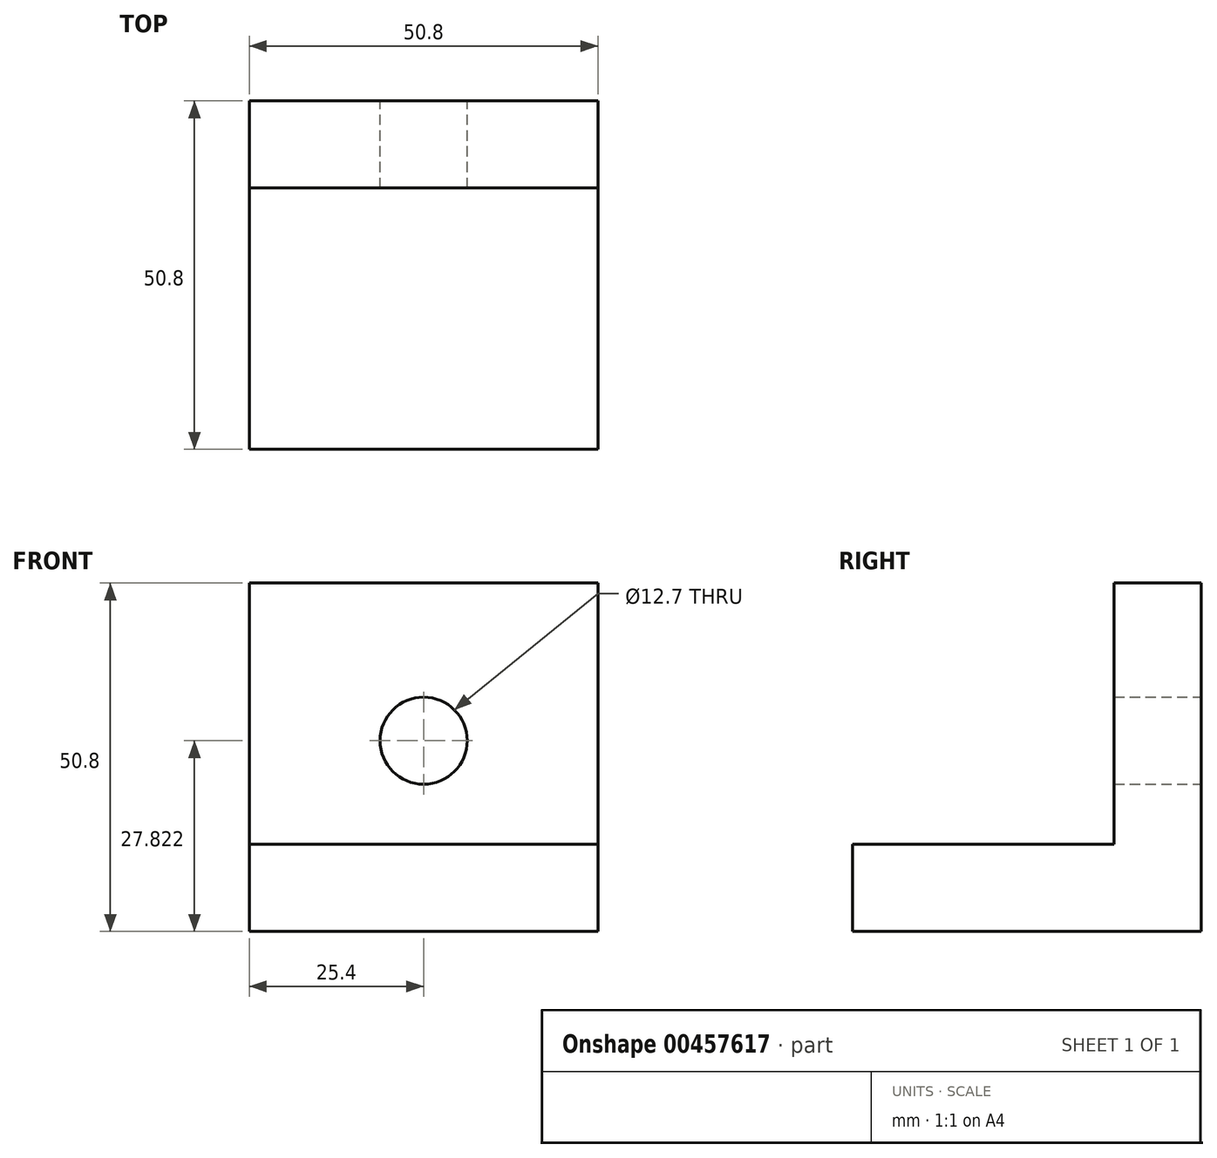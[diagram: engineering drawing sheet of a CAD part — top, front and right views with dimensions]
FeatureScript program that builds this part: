
annotation { "Feature Type Name" : "Feature", "Feature Type Description" : "" }
export const myFeature = defineFeature(function(context is Context, id is Id, definition is map)
    precondition{}
    {
        {
            var Q0;
            Q0=qCreatedBy(makeId("Right.planeOp"),FACE);
            var sketch = newSketch(context, id + "F0", { "sketchPlane" : qUnion([Q0])});
            skLineSegment(sketch, "E0", {"start": v(0, 33.78) * mm, "end": v(0, -17.02) * mm});
            skLineSegment(sketch, "E1", {"start": v(0, -17.02) * mm, "end": v(-50.8, -17.02) * mm});
            skLineSegment(sketch, "E2", {"start": v(-50.8, -17.02) * mm, "end": v(-50.8, -4.32) * mm});
            skLineSegment(sketch, "E3", {"start": v(-50.8, -4.32) * mm, "end": v(-12.7, -4.32) * mm});
            skLineSegment(sketch, "E4", {"start": v(-12.7, -4.32) * mm, "end": v(-12.7, 33.78) * mm});
            skLineSegment(sketch, "E5", {"start": v(-12.7, 33.78) * mm, "end": v(0, 33.78) * mm});
            skSolve(sketch);
        }
        {
            var Q0;
            Q0=qCreatedBy(makeId("Front.planeOp"),FACE);
            var sketch = newSketch(context, id + "F1", { "sketchPlane" : qUnion([Q0])});
            skCircle(sketch, "E6", {"center": v(0, 10.8) * mm, "radius": 6.35 * mm});
            skSolve(sketch);
        }
        {
            var Q0;
            Q0=makeQuery(id+"F0.imprint","IMPRINT",FACE,{"disambiguationData":[TD([[makeQuery(id+"F0.imprint","IMPRINT",EDGE,{"derivedFrom":sQuery(id+"F0.wireOp",EDGE,"E0")}),-1.0]])]});
            extrude(context, id + "F2", {"entities" : qUnion([Q0]), "endBound" : BoundingType.SYMMETRIC, "depth" : 50.8 * mm});
        }
        {
            var Q0;
            Q0=sQuery(id+"F1.wireOp",VERTEX,"E6.center");
            var Q1;
            Q1=makeQuery(id+"F2.opExtrude","SWEPT_BODY",BODY,{"disambiguationData":[OSD([sQuery(id+"F0.wireOp",EDGE,"E0"),sQuery(id+"F0.wireOp",EDGE,"E1"),sQuery(id+"F0.wireOp",EDGE,"E2"),sQuery(id+"F0.wireOp",EDGE,"E3"),sQuery(id+"F0.wireOp",EDGE,"E4"),sQuery(id+"F0.wireOp",EDGE,"E5")])]});
            hole(context, id + "F3", {"style" : HoleStyle.SIMPLE, "endStyle" : HoleEndStyle.THROUGH, "oppositeDirection" : true, "holeDiameter" : 12.7 * mm, "isTappedThrough" : true, "tappedDepth" : 12.7 * mm, "tapClearance" : 3, "locations" : qUnion([Q0]), "scope" : qUnion([Q1])});
        }
    });
